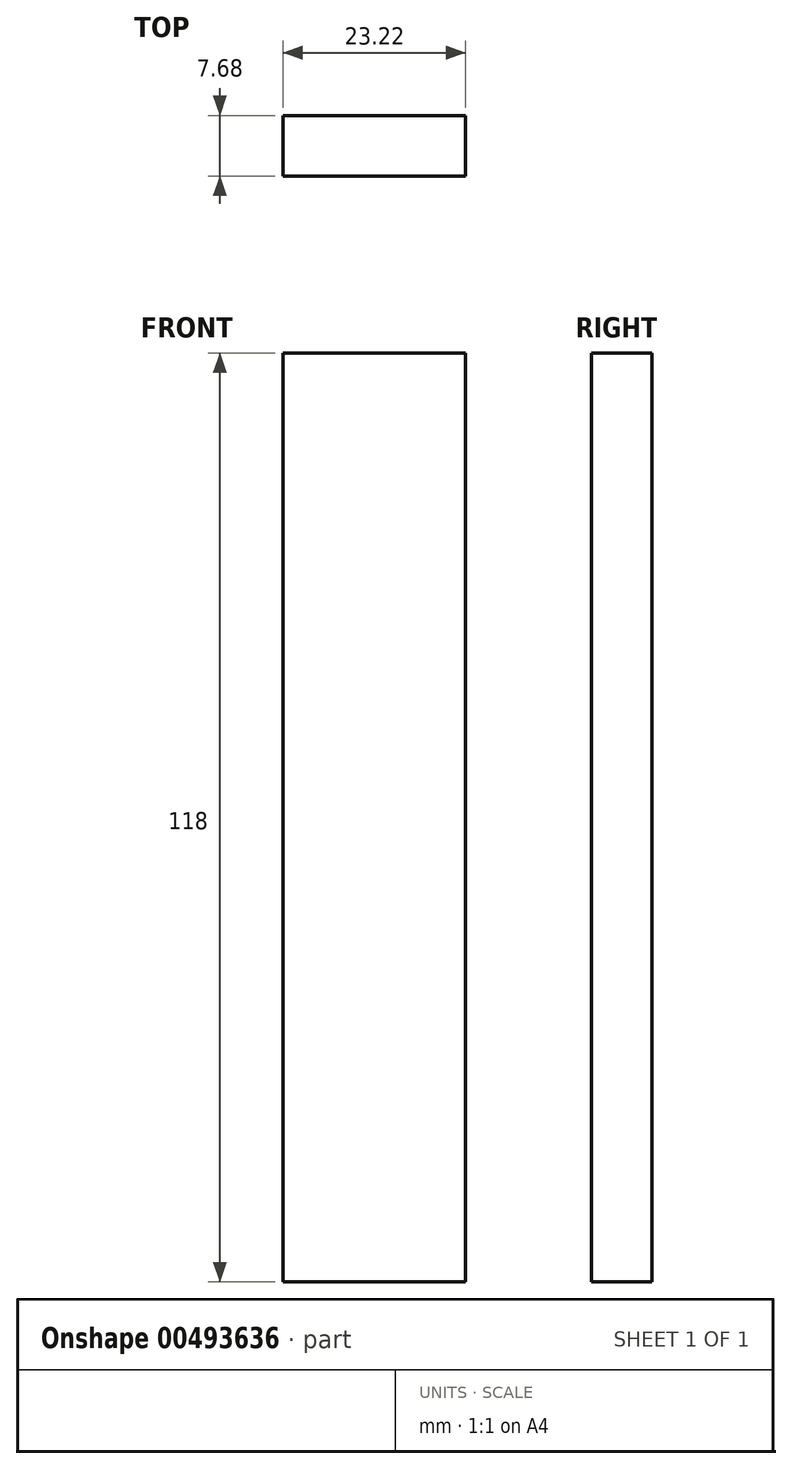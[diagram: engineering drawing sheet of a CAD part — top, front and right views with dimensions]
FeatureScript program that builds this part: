
annotation { "Feature Type Name" : "Feature", "Feature Type Description" : "" }
export const myFeature = defineFeature(function(context is Context, id is Id, definition is map)
    precondition{}
    {
        {
            var Q0;
            Q0=qCreatedBy(makeId("Front.planeOp"),FACE);
            var sketch = newSketch(context, id + "F0", { "sketchPlane" : qUnion([Q0])});
            skLineSegment(sketch, "E0.bottom", {"start": v(-11.61, 59) * mm, "end": v(11.61, 59) * mm});
            skLineSegment(sketch, "E0.top", {"start": v(-11.61, -59) * mm, "end": v(11.61, -59) * mm});
            skLineSegment(sketch, "E0.left", {"start": v(-11.61, 59) * mm, "end": v(-11.61, -59) * mm});
            skLineSegment(sketch, "E0.right", {"start": v(11.61, 59) * mm, "end": v(11.61, -59) * mm});
            skPoint(sketch, "E0.middle", {"position": v(0, 0) * mm});
            skSolve(sketch);
        }
        {
            var Q0;
            Q0=makeQuery(id+"F0.imprint","IMPRINT",FACE,{"disambiguationData":[TD([[makeQuery(id+"F0.imprint","IMPRINT",EDGE,{"derivedFrom":sQuery(id+"F0.wireOp",EDGE,"E0.bottom")}),-1.0]])]});
            extrude(context, id + "F1", {"entities" : qUnion([Q0]), "endBound" : BoundingType.SYMMETRIC, "depth" : 7.67 * mm});
        }
    });
